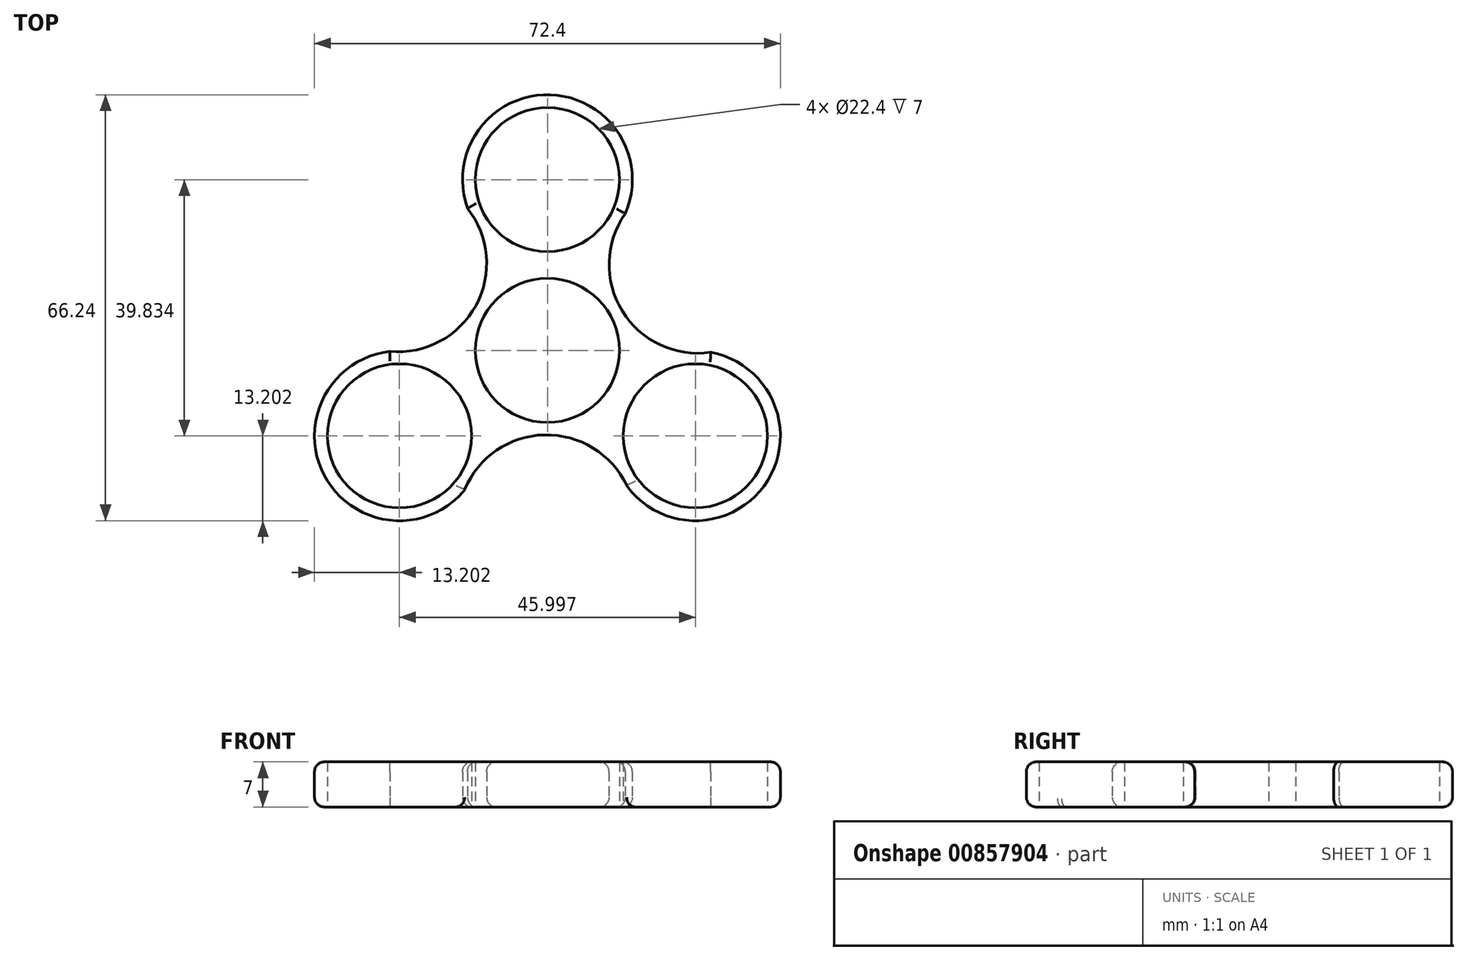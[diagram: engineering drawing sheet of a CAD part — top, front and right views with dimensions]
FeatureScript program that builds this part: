
annotation { "Feature Type Name" : "Feature", "Feature Type Description" : "" }
export const myFeature = defineFeature(function(context is Context, id is Id, definition is map)
    precondition{}
    {
        {
            var Q0;
            Q0=qCreatedBy(makeId("Top.planeOp"),FACE);
            var sketch = newSketch(context, id + "F0", { "sketchPlane" : qUnion([Q0])});
            skCircle(sketch, "E0", {"center": v(0, 0) * mm, "radius": 11.2 * mm});
            skArc(sketch, "E1", {"start": v(-1.08, -13.16) * mm, "mid": v(-0.06, -13.2) * mm, "end": v(0.96, -13.16) * mm});
            skCircle(sketch, "E2", {"center": v(0, 26.56) * mm, "radius": 11.2 * mm});
            skArc(sketch, "E3", {"start": v(10.75, 18.9) * mm, "mid": v(-0.38, 39.75) * mm, "end": v(-10.3, 18.3) * mm});
            skArc(sketch, "E4.1.0", {"start": v(-21.75, -0.14) * mm, "mid": v(-30.51, -24.13) * mm, "end": v(-11.14, -7.49) * mm});
            skCircle(sketch, "E4.1.1", {"center": v(-23, -13.28) * mm, "radius": 11.2 * mm});
            skArc(sketch, "E4.2.0", {"start": v(11, -18.77) * mm, "mid": v(34.62, -19.55) * mm, "end": v(21, -0.23) * mm});
            skCircle(sketch, "E4.2.1", {"center": v(23, -13.28) * mm, "radius": 11.2 * mm});
            skLineSegment(sketch, "E5", {"start": v(0, 0) * mm, "end": v(10.96, 7.36) * mm});
            skLineSegment(sketch, "E6", {"start": v(10.96, 7.36) * mm, "end": v(0, 0) * mm});
            skArc(sketch, "E7", {"start": v(12.1, 21.28) * mm, "mid": v(11.62, 6.13) * mm, "end": v(25.36, -0.3) * mm});
            skArc(sketch, "E8.1.0", {"start": v(-24.48, -0.16) * mm, "mid": v(-11.12, 7) * mm, "end": v(-12.43, 22.1) * mm});
            skArc(sketch, "E8.2.0", {"start": v(12.38, -21.12) * mm, "mid": v(-0.5, -13.13) * mm, "end": v(-12.93, -21.81) * mm});
            skLineSegment(sketch, "E9.trimOffspring", {"start": v(-9.3, -6.25) * mm, "end": v(-12.82, -8.61) * mm});
            skArc(sketch, "E10.trimOffspring", {"start": v(-10.85, 7.52) * mm, "mid": v(-11.4, 6.65) * mm, "end": v(-11.88, 5.75) * mm});
            skArc(sketch, "E11.trimOffspring", {"start": v(11.94, 5.64) * mm, "mid": v(11.46, 6.55) * mm, "end": v(10.92, 7.41) * mm});
            skSolve(sketch);
        }
        {
            var Q0;
            Q0=makeQuery(id+"F0.imprint","IMPRINT",FACE,{"disambiguationData":[TD([[makeQuery(id+"F0.imprint","IMPRINT",EDGE,{"derivedFrom":sQuery(id+"F0.wireOp",EDGE,"E2")}),-1.0]])]});
            var Q1;
            Q1=makeQuery(id+"F0.imprint","IMPRINT",FACE,{"disambiguationData":[TD([[makeQuery(id+"F0.imprint","IMPRINT",EDGE,{"derivedFrom":sQuery(id+"F0.wireOp",EDGE,"E4.2.1")}),-1.0]])]});
            extrude(context, id + "F1", {"entities" : qUnion([Q0, Q1]), "depth" : 7 * mm, "offsetDistance" : 25 * mm});
        }
        {
            var Q0;
            Q0=makeQuery(id+"F1.opExtrude","CAP_EDGE",EDGE,{"disambiguationData":[OSD([sQuery(id+"F0.wireOp",EDGE,"E8.2.0")])],"isStart":false});
            var Q1;
            Q1=makeQuery(id+"F1.opExtrude","CAP_EDGE",EDGE,{"disambiguationData":[OSD([sQuery(id+"F0.wireOp",EDGE,"E8.2.0")])],"isStart":true});
            var Q2;
            Q2=makeQuery(id+"F1.opExtrude","CAP_EDGE",EDGE,{"disambiguationData":[OSD([sQuery(id+"F0.wireOp",EDGE,"E4.1.0")])],"isStart":false});
            var Q3;
            Q3=makeQuery(id+"F1.opExtrude","CAP_EDGE",EDGE,{"disambiguationData":[OSD([sQuery(id+"F0.wireOp",EDGE,"E8.1.0")])],"isStart":false});
            var Q4;
            Q4=makeQuery(id+"F1.opExtrude","CAP_EDGE",EDGE,{"disambiguationData":[OSD([sQuery(id+"F0.wireOp",EDGE,"E3")])],"isStart":false});
            var Q5;
            Q5=makeQuery(id+"F1.opExtrude","CAP_EDGE",EDGE,{"disambiguationData":[OSD([sQuery(id+"F0.wireOp",EDGE,"E7")])],"isStart":false});
            var Q6;
            Q6=makeQuery(id+"F1.opExtrude","CAP_EDGE",EDGE,{"disambiguationData":[OSD([sQuery(id+"F0.wireOp",EDGE,"E4.2.0")])],"isStart":false});
            fillet(context, id + "F2", {"entities" : qUnion([Q0, Q1, Q2, Q3, Q4, Q5, Q6]), "radius" : 1.5 * mm, "tangentPropagation" : true, "allowEdgeOverflow" : false});
        }
        {
            var Q0;
            Q0=makeQuery(id+"F1.opExtrude","CAP_EDGE",EDGE,{"disambiguationData":[OSD([sQuery(id+"F0.wireOp",EDGE,"E4.2.0")])],"isStart":true});
            var Q1;
            Q1=makeQuery(id+"F1.opExtrude","CAP_EDGE",EDGE,{"disambiguationData":[OSD([sQuery(id+"F0.wireOp",EDGE,"E7")])],"isStart":true});
            var Q2;
            Q2=makeQuery(id+"F1.opExtrude","CAP_EDGE",EDGE,{"disambiguationData":[OSD([sQuery(id+"F0.wireOp",EDGE,"E3")])],"isStart":true});
            var Q3;
            Q3=makeQuery(id+"F1.opExtrude","CAP_EDGE",EDGE,{"disambiguationData":[OSD([sQuery(id+"F0.wireOp",EDGE,"E8.1.0")])],"isStart":true});
            var Q4;
            Q4=makeQuery(id+"F1.opExtrude","CAP_EDGE",EDGE,{"disambiguationData":[OSD([sQuery(id+"F0.wireOp",EDGE,"E4.1.0")])],"isStart":true});
            fillet(context, id + "F3", {"entities" : qUnion([Q0, Q1, Q2, Q3, Q4]), "radius" : 1.5 * mm, "tangentPropagation" : true, "allowEdgeOverflow" : false});
        }
    });
